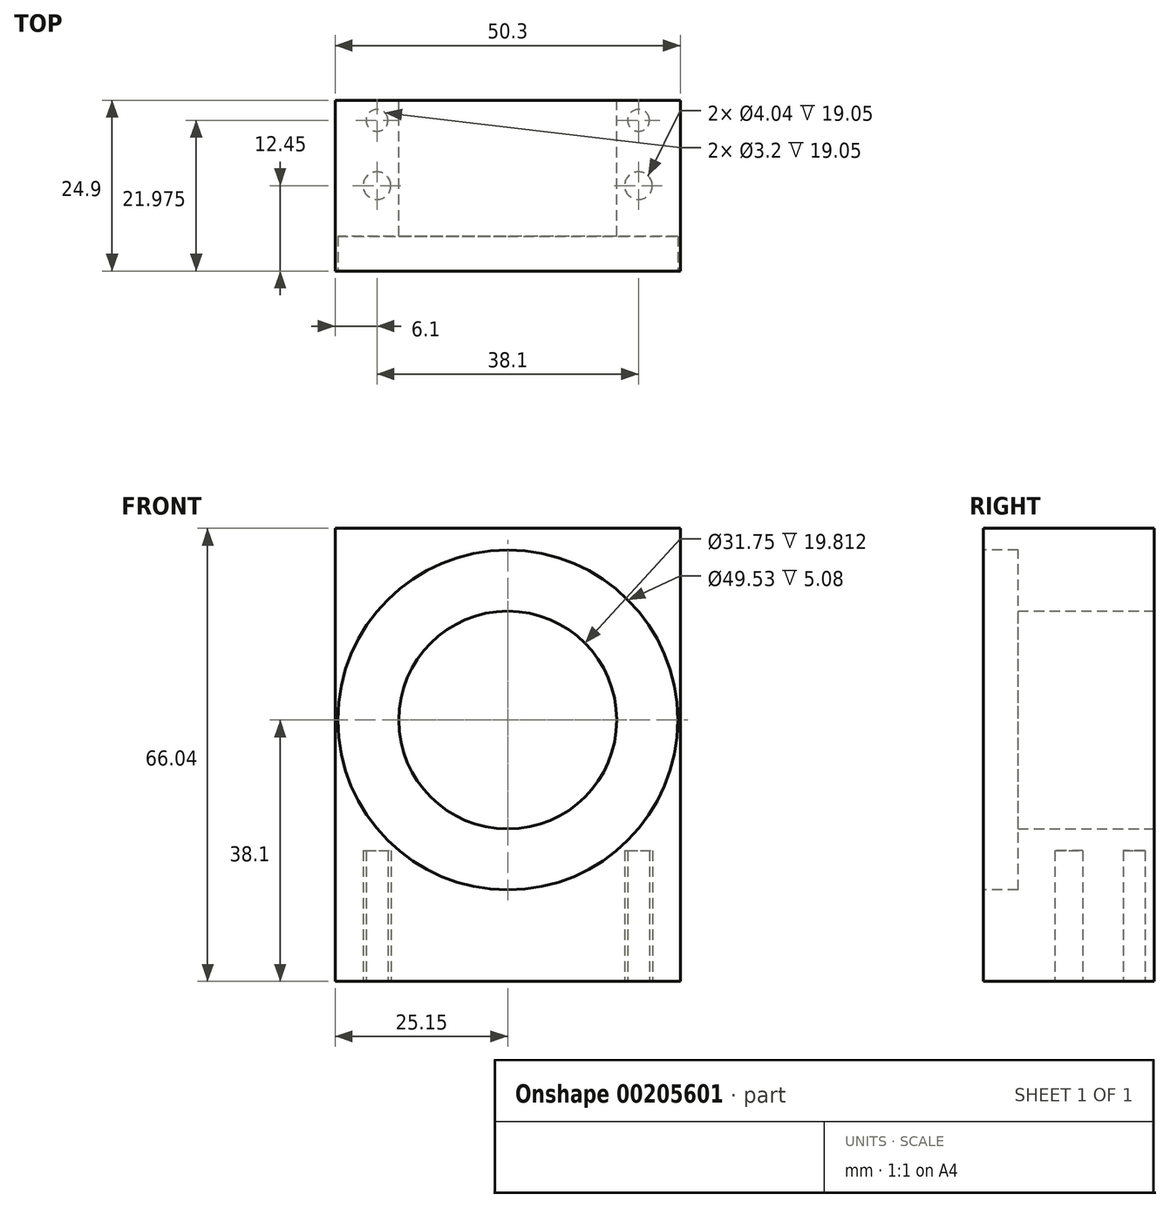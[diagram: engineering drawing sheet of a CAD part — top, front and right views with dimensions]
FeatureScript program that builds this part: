
annotation { "Feature Type Name" : "Feature", "Feature Type Description" : "" }
export const myFeature = defineFeature(function(context is Context, id is Id, definition is map)
    precondition{}
    {
        {
            var Q0;
            Q0=qCreatedBy(makeId("Front.planeOp"),FACE);
            var sketch = newSketch(context, id + "F0", { "sketchPlane" : qUnion([Q0])});
            skLineSegment(sketch, "E0.bottom", {"start": v(-25.15, 27.94) * mm, "end": v(25.15, 27.94) * mm});
            skLineSegment(sketch, "E0.top", {"start": v(-25.15, -38.1) * mm, "end": v(25.15, -38.1) * mm});
            skLineSegment(sketch, "E0.left", {"start": v(-25.15, 27.94) * mm, "end": v(-25.15, -38.1) * mm});
            skLineSegment(sketch, "E0.right", {"start": v(25.15, 27.94) * mm, "end": v(25.15, -38.1) * mm});
            skCircle(sketch, "E1", {"center": v(0, 0) * mm, "radius": 15.88 * mm});
            skSolve(sketch);
        }
        {
            var Q0;
            Q0=qSketchRegion(id+"F0",true);
            extrude(context, id + "F1", {"entities" : qUnion([Q0]), "depth" : 24.9 * mm, "symmetric" : true});
        }
        {
            var Q0;
            Q0=makeQuery(id+"F1.opExtrude","CAP_FACE",FACE,{"disambiguationData":[OSD([sQuery(id+"F0.wireOp",EDGE,"E0.bottom"),sQuery(id+"F0.wireOp",EDGE,"E0.top"),sQuery(id+"F0.wireOp",EDGE,"E0.left"),sQuery(id+"F0.wireOp",EDGE,"E0.right"),sQuery(id+"F0.wireOp",EDGE,"E1")])],"isStart":false});
            var sketch = newSketch(context, id + "F2", { "sketchPlane" : qUnion([Q0])});
            skCircle(sketch, "E2", {"center": v(0, 0) * mm, "radius": 24.77 * mm});
            skSolve(sketch);
        }
        {
            var Q0;
            Q0=qSketchRegion(id+"F2",true);
            extrude(context, id + "F3", {"entities" : qUnion([Q0]), "operationType" : NewBodyOperationType.REMOVE, "oppositeDirection" : true, "depth" : 5.08 * mm});
        }
        {
            var Q0;
            Q0=makeQuery(id+"F1.opExtrude","SWEPT_FACE",FACE,{"disambiguationData":[OSD([sQuery(id+"F0.wireOp",EDGE,"E0.top")])]});
            var sketch = newSketch(context, id + "F4", { "sketchPlane" : qUnion([Q0])});
            skCircle(sketch, "E3", {"center": v(-19.05, 0) * mm, "radius": 2.02 * mm});
            skCircle(sketch, "E4", {"center": v(19.05, 0) * mm, "radius": 2.02 * mm});
            skCircle(sketch, "E5", {"center": v(-19.05, -9.53) * mm, "radius": 1.6 * mm});
            skCircle(sketch, "E6", {"center": v(19.05, -9.52) * mm, "radius": 1.6 * mm});
            skSolve(sketch);
        }
        {
            var Q0;
            Q0=qSketchRegion(id+"F4",true);
            extrude(context, id + "F5", {"entities" : qUnion([Q0]), "operationType" : NewBodyOperationType.REMOVE, "oppositeDirection" : true, "depth" : 19.05 * mm});
        }
    });
